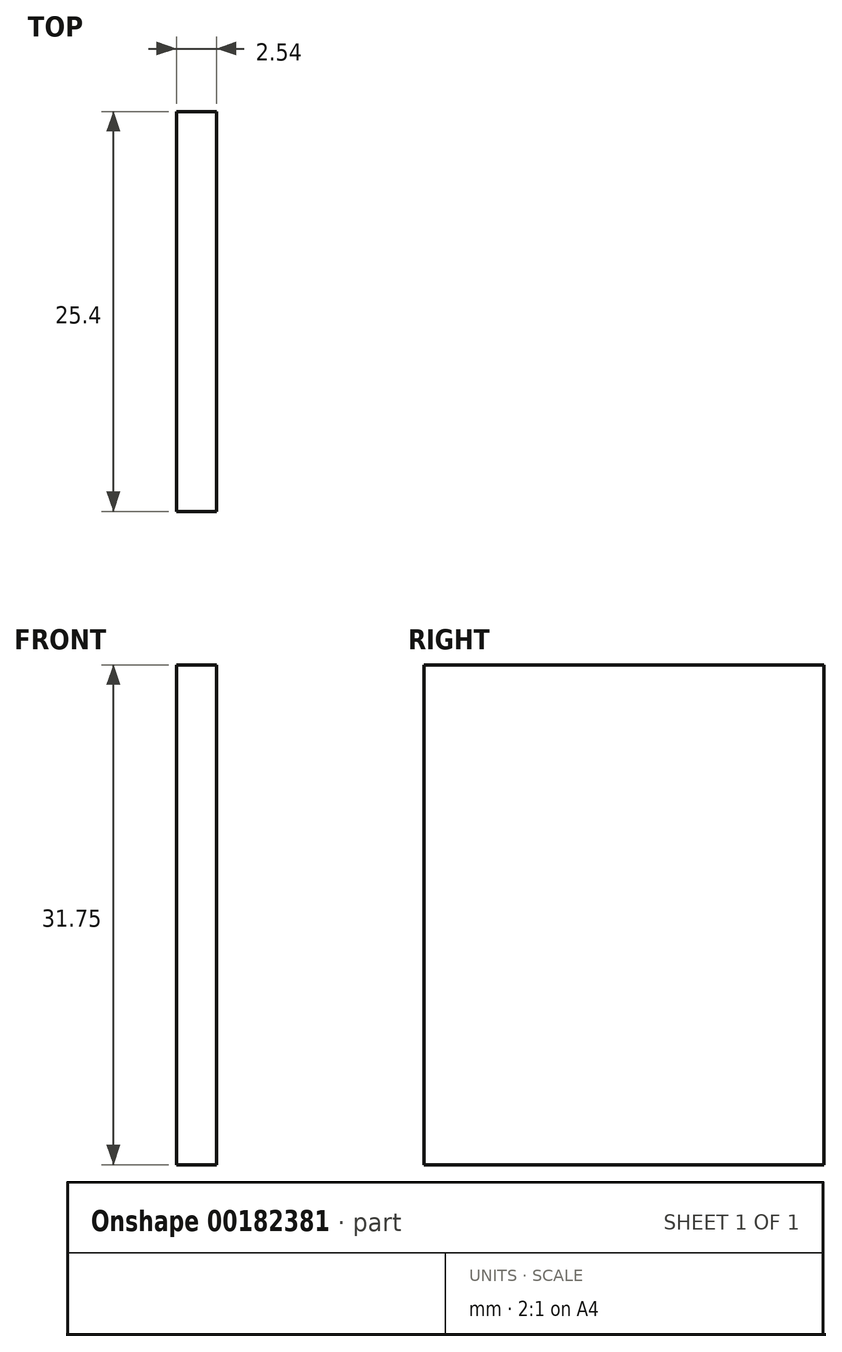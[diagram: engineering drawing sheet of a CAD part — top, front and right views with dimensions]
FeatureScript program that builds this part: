
annotation { "Feature Type Name" : "Feature", "Feature Type Description" : "" }
export const myFeature = defineFeature(function(context is Context, id is Id, definition is map)
    precondition{}
    {
        {
            var Q0;
            Q0=qCreatedBy(makeId("Front.planeOp"),FACE);
            var sketch = newSketch(context, id + "F0", { "sketchPlane" : qUnion([Q0])});
            skLineSegment(sketch, "E0", {"start": v(0, 0) * mm, "end": v(0, 31.75) * mm});
            skLineSegment(sketch, "E1", {"start": v(0, 31.75) * mm, "end": v(2.54, 31.75) * mm});
            skLineSegment(sketch, "E2", {"start": v(2.54, 31.75) * mm, "end": v(2.54, 0) * mm});
            skLineSegment(sketch, "E3", {"start": v(2.54, 0) * mm, "end": v(0, 0) * mm});
            skSolve(sketch);
        }
        {
            var Q0;
            Q0=makeQuery(id+"F0.imprint","IMPRINT",FACE,{"disambiguationData":[TD([[makeQuery(id+"F0.imprint","IMPRINT",EDGE,{"derivedFrom":sQuery(id+"F0.wireOp",EDGE,"E0")}),-1.0]])]});
            extrude(context, id + "F1", {"entities" : qUnion([Q0]), "depth" : 25.4 * mm});
        }
    });
